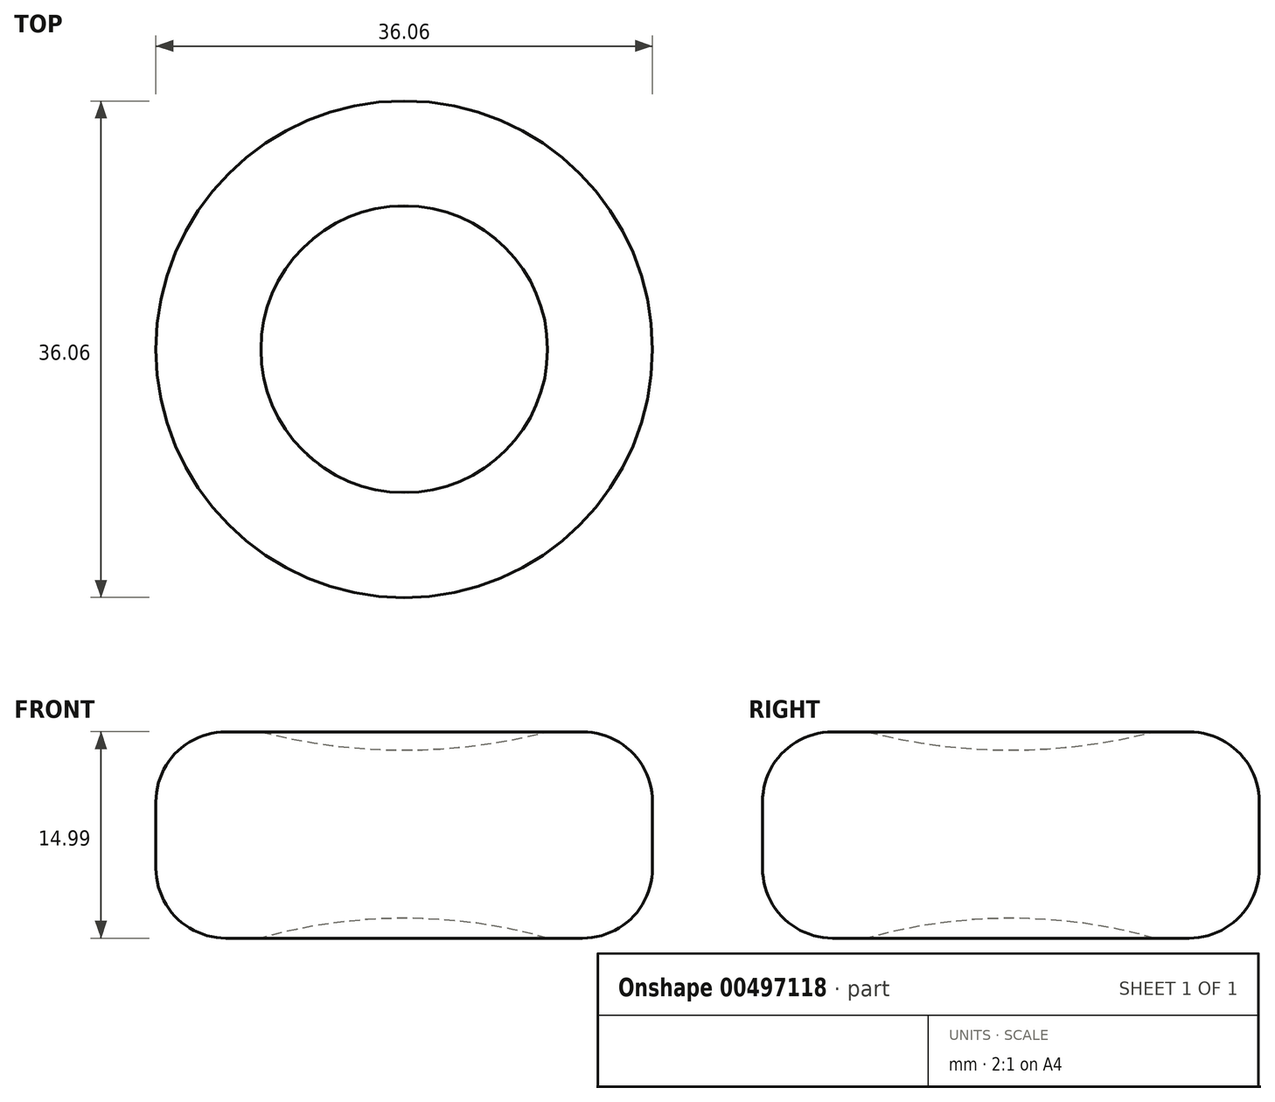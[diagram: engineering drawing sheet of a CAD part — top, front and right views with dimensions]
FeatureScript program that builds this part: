
annotation { "Feature Type Name" : "Feature", "Feature Type Description" : "" }
export const myFeature = defineFeature(function(context is Context, id is Id, definition is map)
    precondition{}
    {
        {
            var Q0;
            Q0=qCreatedBy(makeId("Top.planeOp"),FACE);
            var sketch = newSketch(context, id + "F0", { "sketchPlane" : qUnion([Q0])});
            skCircle(sketch, "E0", {"center": v(0, 0) * mm, "radius": 18.03 * mm});
            skSolve(sketch);
        }
        {
            var Q0;
            Q0=makeQuery(id+"F0.imprint","IMPRINT",FACE,{"disambiguationData":[TD([[makeQuery(id+"F0.imprint","IMPRINT",EDGE,{"derivedFrom":sQuery(id+"F0.wireOp",EDGE,"E0")}),1.0]])]});
            extrude(context, id + "F1", {"entities" : qUnion([Q0]), "depth" : 15 * mm});
        }
        {
            var Q0;
            Q0=makeQuery(id+"F1.opExtrude","SWEPT_FACE",FACE,{"disambiguationData":[OSD([sQuery(id+"F0.wireOp",EDGE,"E0")])]});
            fillet(context, id + "F2", {"entities" : qUnion([Q0]), "radius" : 5.08 * mm, "tangentPropagation" : true, "allowEdgeOverflow" : false});
        }
        {
            var Q0;
            Q0=qCreatedBy(makeId("Right.planeOp"),FACE);
            var sketch = newSketch(context, id + "F3", { "sketchPlane" : qUnion([Q0])});
            skCircle(sketch, "E1", {"center": v(0, 55.16) * mm, "radius": 41.5 * mm});
            skLineSegment(sketch, "E2", {"start": v(53.21, 55.16) * mm, "end": v(-52.7, 55.16) * mm});
            skSolve(sketch);
        }
        {
            var Q0;
            {var subQ0=sQuery(id+"F3.wireOp",EDGE,"E2");var subQ1=sQuery(id+"F3.wireOp",EDGE,"E1");var subQ2=makeQuery(id+"F3.imprint","INTERSECT",VERTEX,{"disambiguationData":[OD(0.0)],"derivedFrom":[subQ1,subQ0]});Q0=makeQuery(id+"F3.imprint","IMPRINT",FACE,{"disambiguationData":[TD([[makeQuery(id+"F3.imprint","IMPRINT",EDGE,{"disambiguationData":[TD([[subQ2,-1.0]])],"derivedFrom":subQ1}),1.0]])]});}
            var Q1;
            Q1=sQuery(id+"F3.wireOp",EDGE,"E2");
            revolve(context, id + "F4", {"operationType" : NewBodyOperationType.REMOVE, "entities" : qUnion([Q0]), "axis" : qUnion([Q1]), "revolveType" : RevolveType.FULL, "oppositeDirection" : true});
        }
        {
            var Q0;
            Q0=qCreatedBy(makeId("Front.planeOp"),FACE);
            var sketch = newSketch(context, id + "F5", { "sketchPlane" : qUnion([Q0])});
            skCircle(sketch, "E3", {"center": v(0, -37.02) * mm, "radius": 38.46 * mm});
            skLineSegment(sketch, "E4", {"start": v(50.28, -37.02) * mm, "end": v(-46.78, -37.02) * mm});
            skSolve(sketch);
        }
        {
            var Q0;
            {var subQ0=sQuery(id+"F5.wireOp",EDGE,"E4");var subQ1=sQuery(id+"F5.wireOp",EDGE,"E3");var subQ2=makeQuery(id+"F5.imprint","INTERSECT",VERTEX,{"disambiguationData":[OD(0.0)],"derivedFrom":[subQ1,subQ0]});Q0=makeQuery(id+"F5.imprint","IMPRINT",FACE,{"disambiguationData":[TD([[makeQuery(id+"F5.imprint","IMPRINT",EDGE,{"disambiguationData":[TD([[subQ2,1.0]])],"derivedFrom":subQ1}),1.0]])]});}
            var Q1;
            Q1=sQuery(id+"F5.wireOp",EDGE,"E4");
            revolve(context, id + "F6", {"operationType" : NewBodyOperationType.REMOVE, "entities" : qUnion([Q0]), "axis" : qUnion([Q1]), "revolveType" : RevolveType.FULL, "oppositeDirection" : true});
        }
    });
